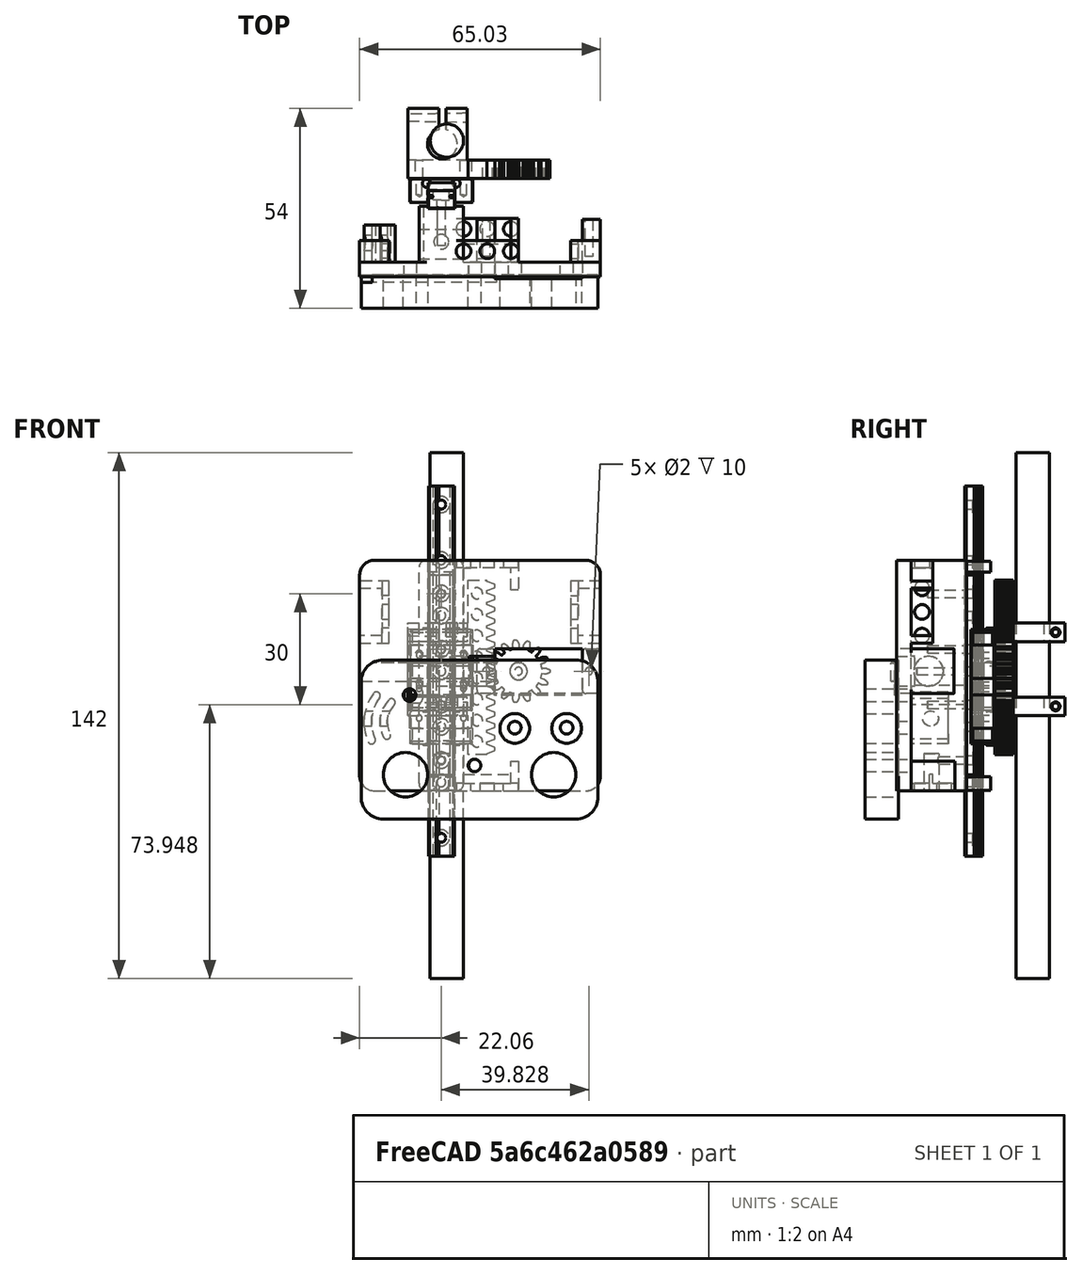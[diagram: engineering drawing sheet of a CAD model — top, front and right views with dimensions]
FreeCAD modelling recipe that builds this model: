
FCSTD DOCUMENT  (FreeCAD 1.0R39109 (Git))
Label: pen_plotter_head
License: All rights reserved
LicenseURL: https://en.wikipedia.org/wiki/All_rights_reserved
objects: Sketcher::SketchObject×36, PartDesign::Pocket×24, PartDesign::Pad×11, Part::Feature×10, PartDesign::LinearPattern×8, PartDesign::Body×4, App::Part×2, Mesh::Feature×2, Part::FeaturePython×2, Part::Box×2, PartDesign::FeatureBase×2, Part::MultiCommon×1, Part::MultiFuse×1, Part::Cylinder×1, PartDesign::PolarPattern×1
note: 220 computed .brp shape members not serialized (recipe doc carries the construction recipe); baked Part::Feature solids carry a one-line shape summary decoded from their .brp

FEATURE [Part::Feature] Part__Feature  label="Carriage-LWL7B"
  Placement = pos=(0,1.55,0.331361) rot=(0,0,1;0rad)
  shape: bbox 16.95 x 6.5 x 13.5 mm, 45 faces (baked)
FEATURE [Part::Feature] Part__Feature001  label="Carriage-LWL7B001"
  Placement = pos=(0,1.55,0.331361) rot=(0,0,1;0rad)
  shape: bbox 16.69 x 6.37 x 3.45 mm, 29 faces (baked)
FEATURE [Part::Feature] Part__Feature002  label="Carriage-LWL7B002"
  Placement = pos=(0,1.55,0.331361) rot=(0,0,1;0rad)
  shape: bbox 16.69 x 6.37 x 0.7 mm, 29 faces (baked)
FEATURE [Part::Feature] Part__Feature003  label="Carriage-LWL7B003"
  Placement = pos=(0,1.55,0.331361) rot=(0,0,1;0rad)
  shape: bbox 2.381 x 2.381 x 0.4 mm, 6 faces (baked)
FEATURE [Part::Feature] Part__Feature004  label="Carriage-LWL7B004"
  Placement = pos=(0,1.55,0.331361) rot=(0,0,1;0rad)
  shape: bbox 2.381 x 2.381 x 0.4 mm, 6 faces (baked)
FEATURE [Part::Feature] Part__Feature005  label="Carriage-LWL7B005"
  Placement = pos=(0,1.55,0.331361) rot=(0,0,1;0rad)
  shape: bbox 16.69 x 6.37 x 3.45 mm, 29 faces (baked)
FEATURE [Part::Feature] Part__Feature006  label="Carriage-LWL7B006"
  Placement = pos=(0,1.55,0.331361) rot=(0,0,1;0rad)
  shape: bbox 16.69 x 6.37 x 0.7 mm, 29 faces (baked)
FEATURE [Part::Feature] Part__Feature007  label="Carriage-LWL7B007"
  Placement = pos=(0,1.55,0.331361) rot=(0,0,1;0rad)
  shape: bbox 2.381 x 2.381 x 0.4 mm, 6 faces (baked)
FEATURE [Part::Feature] Part__Feature008  label="Carriage-LWL7B008"
  Placement = pos=(0,1.55,0.331361) rot=(0,0,1;0rad)
  shape: bbox 2.381 x 2.381 x 0.4 mm, 6 faces (baked)
FEATURE [App::Part] Carriage_LWL7B  label="Carriage-LWL7B009"
  Group = -> [Part__Feature,Part__Feature001,Part__Feature002,Part__Feature003,Part__Feature004,Part__Feature005,Part__Feature006,Part__Feature007,Part__Feature008]
  Origin = -> Origin
FEATURE [Part::Feature] Part__Feature009  label="LinearRail-LWL7B-100mm"
  shape: bbox 7 x 4.8 x 100 mm, 60 faces (baked)
FEATURE [App::Part] LinearRail_LWL7B_Assy  label="LinearRail-LWL7B-Assy"
  Group = -> [Carriage_LWL7B,Part__Feature009]
  Origin = -> Origin001
FEATURE [Mesh::Feature] Servo_SG90  label="Servo-SG90"
  Placement = pos=(37.5,-19,8.9e-15) rot=(0.57735,-0.57735,-0.57735;4.18879rad)
FEATURE [Part::FeaturePython] InvoluteRack  # WARN: FeaturePython — macro-defined, semantics opaque (R4)
  AttacherType = Attacher::AttachEngine3D
  Placement = pos=(11.5,25,-21) rot=(1,0,0;1.5708rad)
  add_endings = true
  beta = 0
  clearance = 0.25
  double_helix = false
  head = 0
  head_fillet = 0
  height = 5
  module = 1
  num_teeth = 15
  pressure_angle = 20
  properties_from_tool = false
  root_fillet = 0
  simplified = false
  thickness = 5
  transverse_pitch = 3.14159
  version = 1.3.0
FEATURE [Part::FeaturePython] InvoluteGear  # WARN: FeaturePython — macro-defined, semantics opaque (R4)
  AttacherType = Attacher::AttachEngine3D
  Placement = pos=(19,25.15,-2) rot=(1,0,0;1.5708rad)
  angular_backlash = 0
  backlash = 0
  beta = 0
  clearance = 0.25
  da = 17
  df = 12.5
  double_helix = false
  dw = 15
  head = 0
  head_fillet = 0
  height = 5
  module = 1
  num_teeth = 15
  numpoints = 20
  pressure_angle = 20
  properties_from_tool = false
  reversed_backlash = false
  root_fillet = 0
  shift = 0
  simple = false
  transverse_pitch = 3.14159
  traverse_module = 1
  undercut = false
  version = 1.3.0
  expr: angular_backlash = backlash / dw * 360 ° / pi
FEATURE [Mesh::Feature] Carriage_Plate_w_Threads
  Placement = pos=(-21.5,-48,24.5) rot=(-1,0,0;1.5708rad)
FEATURE [Part::Box] Box  label="Cube"
  AttacherType = Attacher::AttachEngine3D
  Height = 54
  Length = 25
  Placement = pos=(-13,-6,-19) rot=(0,0,1;0rad)
  Width = 25
FEATURE [Part::MultiCommon] Common
  Placement = pos=(0,0,-9) rot=(0,0,1;0rad)
  Refine = true
  Shapes = -> [LinearRail_LWL7B_Assy,Box]
FEATURE [Part::Box] Box001  label="Cube001"
  AttacherType = Attacher::AttachEngine3D
  Height = 25
  Length = 20
  Placement = pos=(-11,20,-12) rot=(0,0,1;0rad)
  Width = 5
FEATURE [Part::MultiFuse] Fusion
  Placement = pos=(1.6,-12,-5) rot=(0,0,1;0rad)
  Refine = true
  Shapes = -> [Box001,InvoluteRack]
FEATURE [Part::Cylinder] Cylinder  label="Pen"
  Angle = 360
  AttacherType = Attacher::AttachEngine3D
  FirstAngle = 0
  Height = 142
  Placement = pos=(1.5,18.25,-83) rot=(0,0,1;0rad)
  Radius = 4.5
  SecondAngle = 0
FEATURE [PartDesign::FeatureBase] BaseFeature
  BaseFeature = -> InvoluteGear
  Suppressed = false
FEATURE [Sketcher::SketchObject] Sketch
  ArcFitTolerance = 1e-06
  AttachmentSupport = -> [BaseFeature]
  FullyConstrained = true
  MakeInternals = false
  MapMode = 5
  Placement = pos=(0,0,0) rot=(1,0,0;3.14159rad)
  sketch-geometry (1):
    g0: Circle CenterX=0 CenterY=0 CenterZ=0 NormalX=0 NormalY=0 NormalZ=1 AngleXU=0 Radius=2.35
  constraints (2):
    c: Diameter(g0) = 4.7
    c: Coincident(g0,g-1)
FEATURE [PartDesign::Pocket] Pocket
  BaseFeature = -> BaseFeature
  Direction = (0,0,1)
  Length = 3
  Length2 = 5
  Profile = -> Sketch
  ReferenceAxis = -> Sketch [N_Axis]
  Refine = true
  Suppressed = false
  Type = 0
FEATURE [Sketcher::SketchObject] Sketch001
  ArcFitTolerance = 1e-06
  AttachmentSupport = -> [Pocket]
  FullyConstrained = true
  MakeInternals = false
  MapMode = 5
  Placement = pos=(0,0,3) rot=(1,0,0;3.14159rad)
  sketch-geometry (1):
    g0: Circle CenterX=0 CenterY=0 CenterZ=0 NormalX=0 NormalY=0 NormalZ=1 AngleXU=0 Radius=1.05
  constraints (2):
    c: Coincident(g0,g-1)
    c: Diameter(g0) = 2.1
FEATURE [PartDesign::Pocket] Pocket001
  BaseFeature = -> Pocket
  Direction = (0,0,1)
  Length = 2
  Length2 = 5
  Profile = -> Sketch001
  ReferenceAxis = -> Sketch001 [N_Axis]
  Refine = true
  Suppressed = false
  Type = 0
FEATURE [Sketcher::SketchObject] Sketch002
  ArcFitTolerance = 1e-06
  AttachmentSupport = -> [Pocket001]
  ExternalGeometry = -> [Pocket001]
  FullyConstrained = false
  MakeInternals = false
  MapMode = 5
  Placement = pos=(0,0,3) rot=(1,0,0;3.14159rad)
  sketch-geometry (5):
    g0: LineSegment StartX=-0.0912562 StartY=-2.35 StartZ=0 EndX=0.0912562 EndY=-2.35 EndZ=0
    g1: LineSegment StartX=0.0912562 StartY=-2.35 StartZ=0 EndX=0 EndY=-2.19194 EndZ=0
    g2: LineSegment StartX=0 StartY=-2.19194 StartZ=0 EndX=-0.0912562 EndY=-2.35 EndZ=0
    g3: Circle [constr] CenterX=0 CenterY=-2.29731 CenterZ=0 NormalX=0 NormalY=0 NormalZ=1 AngleXU=0 Radius=0.105374
    g4: GeomPoint X=0 Y=-2.35 Z=0
  constraints (12):
    c: Coincident(g0,g1)
    c: Coincident(g1,g2)
    c: Coincident(g2,g0)
    c: Equal(g0,g1)
    c: Equal(g0,g2)
    c: PointOnObject(g0,g3)
    c: PointOnObject(g1,g3)
    c: PointOnObject(g2,g3)
    c: PointOnObject(g1,g-2)
    c: Horizontal(g0)
    c: Symmetric(g0,g0,g4)
    c: PointOnObject(g4,g-3)
FEATURE [PartDesign::Pad] Pad
  BaseFeature = -> Pocket001
  Direction = (0,0,-1)
  Length = 3
  Length2 = 10
  Profile = -> Sketch002
  ReferenceAxis = -> Sketch002 [N_Axis]
  Refine = true
  Suppressed = false
  Type = 0
FEATURE [PartDesign::PolarPattern] PolarPattern
  Angle = 360
  Axis = -> Sketch002 [N_Axis]
  BaseFeature = -> Pad
  Mode = 0
  Occurrences = 21
  Offset = 120
  Originals = -> [Pad]
  Refine = true
  Suppressed = false
  TransformMode = 0
FEATURE [PartDesign::Body] Body  label="Gear"
  AllowCompound = false
  BaseFeature = -> InvoluteGear
  Group = -> [BaseFeature,Sketch,Pocket,Sketch001,Pocket001,Sketch002,Pad,PolarPattern]
  Origin = -> Origin002
  Placement = pos=(20.85,8,-1.8e-15) rot=(1,0,0;4.71239rad)
  Tip = -> PolarPattern
FEATURE [Sketcher::SketchObject] Sketch003
  ArcFitTolerance = 1e-06
  AttachmentSupport = -> [XZ_Plane003]
  FullyConstrained = false
  MakeInternals = false
  MapMode = 5
  Placement = pos=(0,0,0) rot=(1,0,0;1.5708rad)
  sketch-geometry (10):
    g0: LineSegment StartX=-18.0551 StartY=-32.3284 StartZ=0 EndX=38.9721 EndY=-32.3284 EndZ=0
    g1: LineSegment StartX=42.9721 StartY=-28.3284 StartZ=0 EndX=42.9721 EndY=25.9481 EndZ=0
    g2: LineSegment StartX=38.9721 StartY=29.9481 StartZ=0 EndX=-18.0551 EndY=29.9481 EndZ=0
    g3: LineSegment StartX=-22.0551 StartY=25.9481 StartZ=0 EndX=-22.0551 EndY=-28.3284 EndZ=0
    g4: ArcOfCircle CenterX=-18.0551 CenterY=-28.3284 CenterZ=0 NormalX=0 NormalY=0 NormalZ=1 AngleXU=0 Radius=4 StartAngle=3.14159 EndAngle=4.71239
    g5: ArcOfCircle CenterX=38.9721 CenterY=-28.3284 CenterZ=0 NormalX=0 NormalY=0 NormalZ=1 AngleXU=0 Radius=4 StartAngle=4.71239 EndAngle=6.28319
    g6: ArcOfCircle CenterX=38.9721 CenterY=25.9481 CenterZ=0 NormalX=0 NormalY=0 NormalZ=1 AngleXU=0 Radius=4 StartAngle=0 EndAngle=1.5708
    g7: ArcOfCircle CenterX=-18.0551 CenterY=25.9481 CenterZ=0 NormalX=0 NormalY=0 NormalZ=1 AngleXU=0 Radius=4 StartAngle=1.5708 EndAngle=3.14159
    g8: GeomPoint [constr] X=-22.0551 Y=-32.3284 Z=0
    g9: GeomPoint [constr] X=42.9721 Y=29.9481 Z=0
  constraints (20):
    c: Tangent(g0,g4) = -1.5708
    c: Tangent(g0,g5) = -1.5708
    c: Tangent(g1,g5) = -1.5708
    c: Tangent(g1,g6) = -1.5708
    c: Tangent(g2,g6) = -1.5708
    c: Tangent(g2,g7) = -1.5708
    c: Tangent(g3,g7) = -1.5708
    c: Tangent(g3,g4) = -1.5708
    c: Horizontal(g0)
    c: Horizontal(g2)
    c: Vertical(g1)
    c: Vertical(g3)
    c: Equal(g4,g5)
    c: Equal(g5,g6)
    c: Equal(g6,g7)
    c: PointOnObject(g8,g0)
    c: PointOnObject(g8,g3)
    c: PointOnObject(g9,g1)
    c: PointOnObject(g9,g2)
    c: Radius(g5) = 4
FEATURE [PartDesign::Pad] Pad001
  Direction = (0,-1,2e-16)
  Length = 4
  Length2 = 10
  Placement = pos=(0,0,0) rot=(1,0,0;1.5708rad)
  Profile = -> Sketch003
  ReferenceAxis = -> Sketch003 [N_Axis]
  Refine = true
  Suppressed = false
  Type = 0
FEATURE [Sketcher::SketchObject] Sketch004
  ArcFitTolerance = 1e-06
  AttachmentSupport = -> [Pad001]
  FullyConstrained = false
  MakeInternals = false
  MapMode = 5
  Placement = pos=(0,-3e-16,0) rot=(-1,0,0;1.5708rad)
  sketch-geometry (4):
    g0: LineSegment StartX=14.4828 StartY=6.05835 StartZ=0 EndX=14.4828 EndY=-6.05666 EndZ=0
    g1: LineSegment StartX=14.4828 StartY=-6.05666 StartZ=0 EndX=38.0765 EndY=-6.05666 EndZ=0
    g2: LineSegment StartX=38.0765 StartY=-6.05666 StartZ=0 EndX=38.0765 EndY=6.05835 EndZ=0
    g3: LineSegment StartX=38.0765 StartY=6.05835 StartZ=0 EndX=14.4828 EndY=6.05835 EndZ=0
  constraints (8):
    c: Coincident(g0,g1)
    c: Coincident(g1,g2)
    c: Coincident(g2,g3)
    c: Coincident(g3,g0)
    c: Vertical(g0)
    c: Vertical(g2)
    c: Horizontal(g1)
    c: Horizontal(g3)
FEATURE [PartDesign::Pocket] Pocket002
  BaseFeature = -> Pad001
  Direction = (0,-1,-2e-16)
  Length = 5
  Length2 = 5
  Placement = pos=(0,0,0) rot=(1,0,0;1.5708rad)
  Profile = -> Sketch004
  ReferenceAxis = -> Sketch004 [N_Axis]
  Refine = true
  Suppressed = false
  Type = 0
FEATURE [Sketcher::SketchObject] Sketch005
  ArcFitTolerance = 1e-06
  AttachmentSupport = -> [Pocket002]
  ExternalGeometry = -> [Pocket002]
  FullyConstrained = false
  MakeInternals = false
  MapMode = 5
  Placement = pos=(0,-3e-16,0) rot=(-1,0,0;1.5708rad)
  sketch-geometry (22):
    g0: LineSegment StartX=41.9721 StartY=6.05835 StartZ=0 EndX=39.0765 EndY=6.05835 EndZ=0
    g1: LineSegment StartX=38.0765 StartY=5.05835 StartZ=0 EndX=38.0765 EndY=-5.05666 EndZ=0
    g2: LineSegment StartX=39.0765 StartY=-6.05666 StartZ=0 EndX=41.9721 EndY=-6.05666 EndZ=0
    g3: LineSegment StartX=42.9721 StartY=-5.05666 StartZ=0 EndX=42.9721 EndY=5.05835 EndZ=0
    g4: ArcOfCircle CenterX=41.9721 CenterY=5.05835 CenterZ=0 NormalX=0 NormalY=0 NormalZ=1 AngleXU=0 Radius=1 StartAngle=0 EndAngle=1.5708
    g5: ArcOfCircle CenterX=39.0765 CenterY=5.05835 CenterZ=0 NormalX=0 NormalY=0 NormalZ=1 AngleXU=0 Radius=1 StartAngle=1.5708 EndAngle=3.14159
    g6: ArcOfCircle CenterX=39.0765 CenterY=-5.05666 CenterZ=0 NormalX=0 NormalY=0 NormalZ=1 AngleXU=0 Radius=1 StartAngle=3.14159 EndAngle=4.71239
    g7: ArcOfCircle CenterX=41.9721 CenterY=-5.05666 CenterZ=0 NormalX=0 NormalY=0 NormalZ=1 AngleXU=0 Radius=1 StartAngle=4.71239 EndAngle=6.28319
    g8: GeomPoint [constr] X=42.9721 Y=6.05835 Z=0
    g9: GeomPoint [constr] X=38.0765 Y=-6.05666 Z=0
    g10: LineSegment StartX=14.4828 StartY=-5.05666 StartZ=0 EndX=14.4828 EndY=5.05835 EndZ=0
    g11: LineSegment StartX=13.4828 StartY=6.05835 StartZ=0 EndX=10.5872 EndY=6.05835 EndZ=0
    g12: LineSegment StartX=9.58719 StartY=5.05835 StartZ=0 EndX=9.58719 EndY=-5.05666 EndZ=0
    g13: LineSegment StartX=10.5872 StartY=-6.05666 StartZ=0 EndX=13.4828 EndY=-6.05666 EndZ=0
    g14: ArcOfCircle CenterX=13.4828 CenterY=-5.05666 CenterZ=0 NormalX=0 NormalY=0 NormalZ=1 AngleXU=0 Radius=1 StartAngle=4.71239 EndAngle=6.28319
    g15: ArcOfCircle CenterX=13.4828 CenterY=5.05835 CenterZ=0 NormalX=0 NormalY=0 NormalZ=1 AngleXU=0 Radius=1 StartAngle=0 EndAngle=1.5708
    g16: ArcOfCircle CenterX=10.5872 CenterY=5.05835 CenterZ=0 NormalX=0 NormalY=0 NormalZ=1 AngleXU=0 Radius=1 StartAngle=1.5708 EndAngle=3.14159
    g17: ArcOfCircle CenterX=10.5872 CenterY=-5.05666 CenterZ=0 NormalX=0 NormalY=0 NormalZ=1 AngleXU=0 Radius=1 StartAngle=3.14159 EndAngle=4.71239
    g18: GeomPoint [constr] X=14.4828 Y=-6.05666 Z=0
    g19: GeomPoint [constr] X=9.58719 Y=6.05835 Z=0
    g20: LineSegment [constr] StartX=12.084 StartY=-6.05666 StartZ=0 EndX=39.8838 EndY=-6.05666 EndZ=0
    g21: LineSegment [constr] StartX=24.5654 StartY=6.05835 StartZ=0 EndX=40.1569 EndY=6.05835 EndZ=0
  constraints (52):
    c: Tangent(g0,g4) = -1.5708
    c: Tangent(g0,g5) = -1.5708
    c: Tangent(g1,g5) = -1.5708
    c: Tangent(g1,g6) = -1.5708
    c: Tangent(g2,g6) = -1.5708
    c: Tangent(g2,g7) = -1.5708
    c: Tangent(g3,g7) = -1.5708
    c: Tangent(g3,g4) = -1.5708
    c: Horizontal(g0)
    c: Horizontal(g2)
    c: Vertical(g1)
    c: Vertical(g3)
    c: Equal(g4,g5)
    c: Equal(g5,g6)
    c: Equal(g6,g7)
    c: PointOnObject(g8,g0)
    c: PointOnObject(g8,g3)
    c: PointOnObject(g9,g1)
    c: PointOnObject(g9,g2)
    c: Radius(g5) = 1
    c: Tangent(g10,g14) = -1.5708
    c: Tangent(g10,g15) = -1.5708
    c: Tangent(g11,g15) = -1.5708
    c: Tangent(g11,g16) = -1.5708
    c: Tangent(g12,g16) = -1.5708
    c: Tangent(g12,g17) = -1.5708
    c: Tangent(g13,g17) = -1.5708
    c: Tangent(g13,g14) = -1.5708
    c: Vertical(g10)
    c: Vertical(g12)
    c: Horizontal(g11)
    c: Horizontal(g13)
    c: Equal(g14,g15)
    c: Equal(g15,g16)
    c: Equal(g16,g17)
    c: PointOnObject(g18,g10)
    c: PointOnObject(g18,g13)
    c: PointOnObject(g19,g11)
    c: PointOnObject(g19,g12)
    c: Radius(g15) = 1
    c: Equal(g13,g2)
    c: Equal(g10,g1)
    c: PointOnObject(g10,g-4)
    c: PointOnObject(g1,g-3)
    c: PointOnObject(g3,g-5)
    c: PointOnObject(g20,g-6)
    c: Horizontal(g20)
    c: PointOnObject(g13,g20)
    c: PointOnObject(g2,g20)
    c: PointOnObject(g21,g-7)
    c: PointOnObject(g21,g-7)
    c: PointOnObject(g0,g21)
FEATURE [PartDesign::Pad] Pad002
  BaseFeature = -> Pocket002
  Direction = (0,1,2e-16)
  Length = 11.5
  Length2 = 10
  Placement = pos=(0,0,0) rot=(1,0,0;1.5708rad)
  Profile = -> Sketch005
  ReferenceAxis = -> Sketch005 [N_Axis]
  Refine = true
  Suppressed = false
  Type = 0
FEATURE [Sketcher::SketchObject] Sketch006
  ArcFitTolerance = 1e-06
  AttachmentSupport = -> [Pad002]
  ExternalGeometry = -> [Pad002]
  FullyConstrained = true
  MakeInternals = false
  MapMode = 5
  Placement = pos=(0,-4,0) rot=(1,0,0;1.5708rad)
  sketch-geometry (4):
    g0: LineSegment StartX=7.48281 StartY=4 StartZ=0 EndX=7.48281 EndY=-4 EndZ=0
    g1: LineSegment StartX=7.48281 StartY=-4 StartZ=0 EndX=14.4828 EndY=-4 EndZ=0
    g2: LineSegment StartX=14.4828 StartY=-4 StartZ=0 EndX=14.4828 EndY=4 EndZ=0
    g3: LineSegment StartX=14.4828 StartY=4 StartZ=0 EndX=7.48281 EndY=4 EndZ=0
  constraints (12):
    c: Coincident(g0,g1)
    c: Coincident(g1,g2)
    c: Coincident(g2,g3)
    c: Coincident(g3,g0)
    c: Vertical(g0)
    c: Vertical(g2)
    c: Horizontal(g1)
    c: Horizontal(g3)
    c: PointOnObject(g2,g-3)
    c: Distance(g2,g-1) = 4
    c: Distance(g1,g-1) = 4
    c: DistanceX(g3,g3) = 7
FEATURE [PartDesign::Pocket] Pocket003
  BaseFeature = -> Pad002
  Direction = (0,1,-2e-16)
  Length = 5
  Length2 = 5
  Placement = pos=(0,0,0) rot=(1,0,0;1.5708rad)
  Profile = -> Sketch006
  ReferenceAxis = -> Sketch006 [N_Axis]
  Refine = true
  Suppressed = false
  Type = 0
FEATURE [Sketcher::SketchObject] Sketch007
  ArcFitTolerance = 1e-06
  AttachmentSupport = -> [Pocket003]
  ExternalGeometry = -> [Pocket003]
  FullyConstrained = true
  MakeInternals = false
  MapMode = 5
  Placement = pos=(0,-3e-16,0) rot=(-1,0,0;1.5708rad)
  sketch-geometry (10):
    g0: LineSegment StartX=-6 StartY=30.3284 StartZ=0 EndX=-6 EndY=-27.9481 EndZ=0
    g1: LineSegment StartX=-4 StartY=-29.9481 StartZ=0 EndX=4 EndY=-29.9481 EndZ=0
    g2: LineSegment StartX=6 StartY=-27.9481 StartZ=0 EndX=6 EndY=30.3284 EndZ=0
    g3: LineSegment StartX=4 StartY=32.3284 StartZ=0 EndX=-4 EndY=32.3284 EndZ=0
    g4: ArcOfCircle CenterX=-4 CenterY=30.3284 CenterZ=0 NormalX=0 NormalY=0 NormalZ=1 AngleXU=0 Radius=2 StartAngle=1.5708 EndAngle=3.14159
    g5: ArcOfCircle CenterX=-4 CenterY=-27.9481 CenterZ=0 NormalX=0 NormalY=0 NormalZ=1 AngleXU=0 Radius=2 StartAngle=3.14159 EndAngle=4.71239
    g6: ArcOfCircle CenterX=4 CenterY=-27.9481 CenterZ=0 NormalX=0 NormalY=0 NormalZ=1 AngleXU=0 Radius=2 StartAngle=4.71239 EndAngle=6.28319
    g7: ArcOfCircle CenterX=4 CenterY=30.3284 CenterZ=0 NormalX=0 NormalY=0 NormalZ=1 AngleXU=0 Radius=2 StartAngle=0 EndAngle=1.5708
    g8: GeomPoint [constr] X=-6 Y=32.3284 Z=0
    g9: GeomPoint [constr] X=6 Y=-29.9481 Z=0
  constraints (24):
    c: Tangent(g0,g4) = -1.5708
    c: Tangent(g0,g5) = -1.5708
    c: Tangent(g1,g5) = -1.5708
    c: Tangent(g1,g6) = -1.5708
    c: Tangent(g2,g6) = -1.5708
    c: Tangent(g2,g7) = -1.5708
    c: Tangent(g3,g7) = -1.5708
    c: Tangent(g3,g4) = -1.5708
    c: Vertical(g0)
    c: Vertical(g2)
    c: Horizontal(g1)
    c: Horizontal(g3)
    c: Equal(g4,g5)
    c: Equal(g5,g6)
    c: Equal(g6,g7)
    c: PointOnObject(g8,g0)
    c: PointOnObject(g8,g3)
    c: PointOnObject(g9,g1)
    c: PointOnObject(g9,g2)
    c: Radius(g5) = 2
    c: PointOnObject(g3,g-3)
    c: PointOnObject(g1,g-4)
    c: Distance(g-2,g2) = 6
    c: Distance(g-2,g0) = 6
FEATURE [PartDesign::Pad] Pad003
  BaseFeature = -> Pocket003
  Direction = (0,1,2e-16)
  Length = 15
  Length2 = 10
  Placement = pos=(0,0,0) rot=(1,0,0;1.5708rad)
  Profile = -> Sketch007
  ReferenceAxis = -> Sketch007 [N_Axis]
  Refine = true
  Suppressed = false
  Type = 0
FEATURE [Sketcher::SketchObject] Sketch008
  ArcFitTolerance = 1e-06
  AttachmentSupport = -> [Pad003]
  FullyConstrained = false
  MakeInternals = false
  MapMode = 5
  Placement = pos=(-6,0,0) rot=(0.707107,0,-0.707107;3.14159rad)
  sketch-geometry (1):
    g0: Circle CenterX=0 CenterY=-4.67716 CenterZ=0 NormalX=0 NormalY=0 NormalZ=1 AngleXU=0 Radius=4
  constraints (2):
    c: PointOnObject(g0,g-2)
    c: Diameter(g0) = 8
FEATURE [PartDesign::Pocket] Pocket004
  BaseFeature = -> Pad003
  Direction = (1,0,2e-16)
  Length = 12
  Length2 = 5
  Placement = pos=(0,0,0) rot=(1,0,0;1.5708rad)
  Profile = -> Sketch008
  ReferenceAxis = -> Sketch008 [N_Axis]
  Refine = true
  Suppressed = false
  Type = 0
FEATURE [Sketcher::SketchObject] Sketch009
  ArcFitTolerance = 1e-06
  AttachmentSupport = -> [Pocket004]
  FullyConstrained = false
  MakeInternals = false
  MapMode = 5
  Placement = pos=(0,0,29.9481) rot=(0,0,1;3.14159rad)
  sketch-geometry (4):
    g0: LineSegment StartX=-3.63498 StartY=-14.4346 StartZ=0 EndX=-3.63498 EndY=-15.0307 EndZ=0
    g1: LineSegment StartX=-3.63498 StartY=-15.0307 StartZ=0 EndX=3.61502 EndY=-15.0307 EndZ=0
    g2: LineSegment StartX=3.61502 StartY=-15.0307 StartZ=0 EndX=3.61502 EndY=-14.4346 EndZ=0
    g3: LineSegment StartX=3.61502 StartY=-14.4346 StartZ=0 EndX=-3.63498 EndY=-14.4346 EndZ=0
  constraints (9):
    c: Coincident(g0,g1)
    c: Coincident(g1,g2)
    c: Coincident(g2,g3)
    c: Coincident(g3,g0)
    c: Vertical(g0)
    c: Vertical(g2)
    c: Horizontal(g1)
    c: Horizontal(g3)
    c: DistanceX(g3,g3) = 7.25
FEATURE [PartDesign::Pocket] Pocket005
  BaseFeature = -> Pocket004
  Direction = (0,0,-1)
  Length = 1000
  Length2 = 5
  Placement = pos=(0,0,0) rot=(1,0,0;1.5708rad)
  Profile = -> Sketch009
  ReferenceAxis = -> Sketch009 [N_Axis]
  Refine = true
  Suppressed = false
  Type = 0
FEATURE [Sketcher::SketchObject] Sketch010
  ArcFitTolerance = 1e-06
  AttachmentSupport = -> [Pocket005]
  ExternalGeometry = -> [Pocket005]
  FullyConstrained = true
  MakeInternals = false
  MapMode = 5
  Placement = pos=(0,14.4346,-3.2e-15) rot=(-1,0,0;1.5708rad)
  sketch-geometry (1):
    g0: Circle CenterX=0 CenterY=-20.9481 CenterZ=0 NormalX=0 NormalY=0 NormalZ=1 AngleXU=0 Radius=1
  constraints (3):
    c: PointOnObject(g0,g-2)
    c: Distance(g0,g-3) = 9
    c: Diameter(g0) = 2
FEATURE [PartDesign::Pocket] Pocket006
  BaseFeature = -> Pocket005
  Direction = (0,-1,-2e-16)
  Length = 10
  Length2 = 5
  Placement = pos=(0,0,0) rot=(1,0,0;1.5708rad)
  Profile = -> Sketch010
  ReferenceAxis = -> Sketch010 [N_Axis]
  Refine = true
  Suppressed = false
  Type = 0
FEATURE [PartDesign::LinearPattern] LinearPattern
  BaseFeature = -> Pocket006
  Direction = -> Sketch010 [V_Axis]
  Length = 45
  Mode = 0
  Occurrences = 4
  Offset = 15
  Originals = -> [Pocket006]
  Placement = pos=(0,0,0) rot=(1,0,0;1.5708rad)
  Refine = true
  Suppressed = false
  TransformMode = 0
FEATURE [Sketcher::SketchObject] Sketch011
  ArcFitTolerance = 1e-06
  AttachmentSupport = -> [LinearPattern]
  FullyConstrained = false
  MakeInternals = false
  MapMode = 5
  Placement = pos=(0,11.5,0) rot=(-1,0,0;1.5708rad)
  sketch-geometry (2):
    g0: Circle CenterX=39.8284 CenterY=0 CenterZ=0 NormalX=0 NormalY=0 NormalZ=1 AngleXU=0 Radius=1
    g1: Circle CenterX=12.1284 CenterY=0 CenterZ=0 NormalX=0 NormalY=0 NormalZ=1 AngleXU=0 Radius=1
  constraints (5):
    c: PointOnObject(g0,g-1)
    c: Diameter(g0) = 2
    c: PointOnObject(g1,g-1)
    c: Equal(g1,g0)
    c: DistanceX(g1,g0) = 27.7
FEATURE [PartDesign::Pocket] Pocket007
  BaseFeature = -> LinearPattern
  Direction = (0,-1,-2e-16)
  Length = 10
  Length2 = 5
  Placement = pos=(0,0,0) rot=(1,0,0;1.5708rad)
  Profile = -> Sketch011
  ReferenceAxis = -> Sketch011 [N_Axis]
  Refine = true
  Suppressed = false
  Type = 0
FEATURE [Sketcher::SketchObject] Sketch012
  ArcFitTolerance = 1e-06
  AttachmentSupport = -> [Pocket007]
  ExternalGeometry = -> [Pocket007]
  FullyConstrained = false
  MakeInternals = false
  MapMode = 5
  Placement = pos=(0,-3e-16,0) rot=(-1,0,0;1.5708rad)
  sketch-geometry (33):
    g0: LineSegment StartX=42.9721 StartY=-7.59545 StartZ=0 EndX=42.9721 EndY=-9.59545 EndZ=0
    g1: LineSegment StartX=42.9721 StartY=-9.59545 StartZ=0 EndX=36.9721 EndY=-9.59545 EndZ=0
    g2: LineSegment StartX=36.9721 StartY=-9.59545 StartZ=0 EndX=36.9721 EndY=-22.3954 EndZ=0
    g3: LineSegment StartX=36.9721 StartY=-22.3954 StartZ=0 EndX=42.9721 EndY=-22.3954 EndZ=0
    g4: LineSegment StartX=42.9721 StartY=-22.3954 StartZ=0 EndX=42.9721 EndY=-24.3954 EndZ=0
    g5: LineSegment StartX=42.9721 StartY=-24.3954 StartZ=0 EndX=34.9721 EndY=-24.3954 EndZ=0
    g6: LineSegment StartX=34.9721 StartY=-24.3954 StartZ=0 EndX=34.9721 EndY=-7.59545 EndZ=0
    g7: LineSegment StartX=34.9721 StartY=-7.59545 StartZ=0 EndX=42.9721 EndY=-7.59545 EndZ=0
    g8: LineSegment StartX=-22.0551 StartY=-7.59545 StartZ=0 EndX=-14.0551 EndY=-7.59545 EndZ=0
    g9: LineSegment StartX=-14.0551 StartY=-7.59545 StartZ=0 EndX=-14.0551 EndY=-24.3954 EndZ=0
    g10: LineSegment StartX=-14.0551 StartY=-24.3954 StartZ=0 EndX=-22.0551 EndY=-24.3954 EndZ=0
    g11: LineSegment StartX=-22.0551 StartY=-24.3954 StartZ=0 EndX=-22.0551 EndY=-22.3954 EndZ=0
    g12: LineSegment StartX=-22.0551 StartY=-22.3954 StartZ=0 EndX=-16.0551 EndY=-22.3954 EndZ=0
    g13: LineSegment StartX=-16.0551 StartY=-22.3954 StartZ=0 EndX=-16.0551 EndY=-9.59545 EndZ=0
    g14: LineSegment StartX=-16.0551 StartY=-9.59545 StartZ=0 EndX=-22.0551 EndY=-9.59545 EndZ=0
    g15: LineSegment StartX=-22.0551 StartY=-9.59545 StartZ=0 EndX=-22.0551 EndY=-7.59545 EndZ=0
    g16: LineSegment [constr] StartX=42.9721 StartY=-24.3954 StartZ=0 EndX=-22.0551 EndY=-24.3954 EndZ=0
    g17: LineSegment StartX=4 StartY=32.3284 StartZ=0 EndX=4 EndY=24.3284 EndZ=0
    g18: LineSegment StartX=4 StartY=24.3284 StartZ=0 EndX=6 EndY=24.3284 EndZ=0
    g19: LineSegment StartX=6 StartY=24.3284 StartZ=0 EndX=6 EndY=30.3284 EndZ=0
    g20: LineSegment StartX=6 StartY=30.3284 StartZ=0 EndX=18.8 EndY=30.3284 EndZ=0
    g21: LineSegment StartX=18.8 StartY=30.3284 StartZ=0 EndX=18.8 EndY=24.3284 EndZ=0
    g22: LineSegment StartX=18.8 StartY=24.3284 StartZ=0 EndX=20.8 EndY=24.3284 EndZ=0
    g23: LineSegment StartX=4 StartY=32.3284 StartZ=0 EndX=20.8 EndY=32.3284 EndZ=0
    g24: LineSegment StartX=20.8 StartY=24.3284 StartZ=0 EndX=20.8 EndY=32.3284 EndZ=0
    g25: LineSegment StartX=4 StartY=-21.9481 StartZ=0 EndX=4 EndY=-29.9481 EndZ=0
    g26: LineSegment StartX=4 StartY=-29.9481 StartZ=0 EndX=20.8 EndY=-29.9481 EndZ=0
    g27: LineSegment StartX=20.8 StartY=-29.9481 StartZ=0 EndX=20.8 EndY=-21.9481 EndZ=0
    g28: LineSegment StartX=20.8 StartY=-21.9481 StartZ=0 EndX=18.8 EndY=-21.9481 EndZ=0
    g29: LineSegment StartX=18.8 StartY=-21.9481 StartZ=0 EndX=18.8 EndY=-27.9481 EndZ=0
    g30: LineSegment StartX=18.8 StartY=-27.9481 StartZ=0 EndX=6 EndY=-27.9481 EndZ=0
    g31: LineSegment StartX=6 StartY=-27.9481 StartZ=0 EndX=6 EndY=-21.9481 EndZ=0
    g32: LineSegment StartX=6 StartY=-21.9481 StartZ=0 EndX=4 EndY=-21.9481 EndZ=0
  constraints (98):
    c: Coincident(g0,g1)
    c: Horizontal(g1)
    c: Coincident(g1,g2)
    c: Coincident(g2,g3)
    c: Horizontal(g3)
    c: Coincident(g3,g4)
    c: Coincident(g4,g5)
    c: Coincident(g5,g6)
    c: Vertical(g6)
    c: Coincident(g6,g7)
    c: Coincident(g7,g0)
    c: PointOnObject(g0,g-3)
    c: PointOnObject(g0,g-3)
    c: PointOnObject(g3,g-3)
    c: PointOnObject(g4,g-3)
    c: Parallel(g-3,g2)
    c: Parallel(g3,g5)
    c: Parallel(g5,g7)
    c: Equal(g0,g4)
    c: DistanceY(g2,g2) = 12.8
    c: DistanceY(g6,g6) = 16.8
    c: Distance(g6,g2) = 2
    c: DistanceX(g3,g3) = 6
    c: Horizontal(g8)
    c: Coincident(g8,g9)
    c: Vertical(g9)
    c: Coincident(g9,g10)
    c: Horizontal(g10)
    c: Coincident(g10,g11)
    c: Vertical(g11)
    c: Coincident(g11,g12)
    c: Horizontal(g12)
    c: Coincident(g12,g13)
    c: Vertical(g13)
    c: Coincident(g13,g14)
    c: Horizontal(g14)
    c: Coincident(g14,g15)
    c: Coincident(g15,g8)
    c: Parallel(g15,g11)
    c: Equal(g15,g11)
    c: Equal(g11,g0)
    c: Equal(g13,g2)
    c: Equal(g8,g7)
    c: Equal(g14,g1)
    c: Equal(g12,g3)
    c: PointOnObject(g8,g-4)
    c: Coincident(g16,g4)
    c: PointOnObject(g16,g11)
    c: Horizontal(g16)
    c: PointOnObject(g9,g16)
    c: PointOnObject(g17,g-5)
    c: Vertical(g17)
    c: Coincident(g17,g18)
    c: Horizontal(g18)
    c: Coincident(g18,g19)
    c: Vertical(g19)
    c: Coincident(g19,g20)
    c: Horizontal(g20)
    c: Coincident(g20,g21)
    c: Vertical(g21)
    c: Coincident(g21,g22)
    c: Horizontal(g22)
    c: Equal(g20,g2)
    c: Coincident(g23,g17)
    c: PointOnObject(g23,g-5)
    c: Coincident(g24,g22)
    c: Coincident(g24,g23)
    c: Parallel(g24,g17)
    c: Equal(g22,g18)
    c: Equal(g6,g23)
    c: Equal(g24,g7)
    c: Equal(g19,g21)
    c: Distance(g23,g20) = 2
    c: Vertical(g25)
    c: Coincident(g25,g26)
    c: Horizontal(g26)
    c: Coincident(g26,g27)
    c: Vertical(g27)
    c: Coincident(g27,g28)
    c: Horizontal(g28)
    c: Coincident(g28,g29)
    c: Vertical(g29)
    c: Coincident(g29,g30)
    c: Horizontal(g30)
    c: Coincident(g30,g31)
    c: Vertical(g31)
    c: Coincident(g31,g32)
    c: Coincident(g32,g25)
    c: Equal(g29,g3)
    c: Equal(g3,g31)
    c: Equal(g6,g26)
    c: Equal(g30,g2)
    c: Equal(g32,g28)
    c: Parallel(g32,g28)
    c: Equal(g27,g10)
    c: PointOnObject(g25,g-6)
    c: PointOnObject(g18,g-7)
    c: PointOnObject(g31,g-7)
FEATURE [PartDesign::Pad] Pad004
  BaseFeature = -> Pocket007
  Direction = (0,1,2e-16)
  Length = 5.8
  Length2 = 10
  Placement = pos=(0,0,0) rot=(1,0,0;1.5708rad)
  Profile = -> Sketch012
  ReferenceAxis = -> Sketch012 [N_Axis]
  Refine = true
  Suppressed = false
  Type = 0
FEATURE [Sketcher::SketchObject] Sketch013
  ArcFitTolerance = 1e-06
  AttachmentSupport = -> [Pad004]
  ExternalGeometry = -> [Pad004]
  FullyConstrained = true
  MakeInternals = false
  MapMode = 5
  Placement = pos=(36.9721,0,0) rot=(0.707107,0,0.707107;3.14159rad)
  sketch-geometry (1):
    g0: Circle CenterX=9.59545 CenterY=-2.9 CenterZ=0 NormalX=0 NormalY=0 NormalZ=1 AngleXU=0 Radius=2
  constraints (4):
    c: Diameter(g0) = 4
    c: PointOnObject(g0,g-3)
    c: Distance(g-3) = 5.8
    c: DistanceY(g0,g-3) = 2.9
FEATURE [PartDesign::Pocket] Pocket008
  BaseFeature = -> Pad004
  Direction = (-1,0,2e-16)
  Length = 5
  Length2 = 5
  Placement = pos=(0,0,0) rot=(1,0,0;1.5708rad)
  Profile = -> Sketch013
  ReferenceAxis = -> Sketch013 [N_Axis]
  Refine = true
  Suppressed = false
  Type = 0
FEATURE [PartDesign::LinearPattern] LinearPattern001
  BaseFeature = -> Pocket008
  Direction = -> Sketch013 [H_Axis]
  Length = 12.8
  Mode = 0
  Occurrences = 3
  Offset = 6.4
  Originals = -> [Pocket008]
  Placement = pos=(0,0,0) rot=(1,0,0;1.5708rad)
  Refine = true
  Suppressed = false
  TransformMode = 0
FEATURE [Sketcher::SketchObject] Sketch014
  ArcFitTolerance = 1e-06
  AttachmentSupport = -> [LinearPattern001]
  ExternalGeometry = -> [LinearPattern001]
  FullyConstrained = true
  MakeInternals = false
  MapMode = 5
  Placement = pos=(-16.0551,0,0) rot=(0.707107,0,-0.707107;3.14159rad)
  sketch-geometry (1):
    g0: Circle CenterX=-22.3954 CenterY=-2.9 CenterZ=0 NormalX=0 NormalY=0 NormalZ=1 AngleXU=0 Radius=2
  constraints (2):
    c: Diameter(g0) = 4
    c: Symmetric(g-3,g-3,g0)
FEATURE [PartDesign::Pocket] Pocket009
  BaseFeature = -> LinearPattern001
  Direction = (1,0,2e-16)
  Length = 5
  Length2 = 5
  Placement = pos=(0,0,0) rot=(1,0,0;1.5708rad)
  Profile = -> Sketch014
  ReferenceAxis = -> Sketch014 [N_Axis]
  Refine = true
  Suppressed = false
  Type = 0
FEATURE [PartDesign::LinearPattern] LinearPattern002
  BaseFeature = -> Pocket009
  Direction = -> Sketch014 [H_Axis]
  Length = 12.8
  Mode = 0
  Occurrences = 3
  Offset = 6.4
  Originals = -> [Pocket009]
  Placement = pos=(0,0,0) rot=(1,0,0;1.5708rad)
  Refine = true
  Suppressed = false
  TransformMode = 0
FEATURE [Sketcher::SketchObject] Sketch015
  ArcFitTolerance = 1e-06
  AttachmentSupport = -> [LinearPattern002]
  ExternalGeometry = -> [LinearPattern002]
  FullyConstrained = true
  MakeInternals = false
  MapMode = 5
  Placement = pos=(0,0,-30.3284) rot=(0,0,1;3.14159rad)
  sketch-geometry (1):
    g0: Circle CenterX=-18.8 CenterY=-2.9 CenterZ=0 NormalX=0 NormalY=0 NormalZ=1 AngleXU=0 Radius=2
  constraints (2):
    c: Diameter(g0) = 4
    c: Symmetric(g-3,g-3,g0)
FEATURE [PartDesign::Pocket] Pocket010
  BaseFeature = -> LinearPattern002
  Direction = (0,0,-1)
  Length = 5
  Length2 = 5
  Placement = pos=(0,0,0) rot=(1,0,0;1.5708rad)
  Profile = -> Sketch015
  ReferenceAxis = -> Sketch015 [N_Axis]
  Refine = true
  Suppressed = false
  Type = 0
FEATURE [PartDesign::LinearPattern] LinearPattern003
  BaseFeature = -> Pocket010
  Direction = -> Sketch015 [H_Axis]
  Length = 12.8
  Mode = 0
  Occurrences = 3
  Offset = 6.4
  Originals = -> [Pocket010]
  Placement = pos=(0,0,0) rot=(1,0,0;1.5708rad)
  Refine = true
  Suppressed = false
  TransformMode = 0
FEATURE [Sketcher::SketchObject] Sketch016
  ArcFitTolerance = 1e-06
  AttachmentSupport = -> [LinearPattern003]
  ExternalGeometry = -> [LinearPattern003]
  FullyConstrained = true
  MakeInternals = false
  MapMode = 5
  Placement = pos=(0,0,27.9481) rot=(1,0,0;3.14159rad)
  sketch-geometry (1):
    g0: Circle CenterX=18.8 CenterY=-2.9 CenterZ=0 NormalX=0 NormalY=0 NormalZ=1 AngleXU=0 Radius=2
  constraints (2):
    c: Diameter(g0) = 4
    c: Symmetric(g-3,g-3,g0)
FEATURE [PartDesign::Pocket] Pocket011
  BaseFeature = -> LinearPattern003
  Direction = (0,0,1)
  Length = 5
  Length2 = 5
  Placement = pos=(0,0,0) rot=(1,0,0;1.5708rad)
  Profile = -> Sketch016
  ReferenceAxis = -> Sketch016 [N_Axis]
  Refine = true
  Suppressed = false
  Type = 0
FEATURE [PartDesign::LinearPattern] LinearPattern004
  BaseFeature = -> Pocket011
  Direction = -> Sketch016 [H_Axis]
  Length = 12.8
  Mode = 0
  Occurrences = 3
  Offset = 6.4
  Originals = -> [Pocket011]
  Placement = pos=(0,0,0) rot=(1,0,0;1.5708rad)
  Refine = true
  Reversed = true
  Suppressed = false
  TransformMode = 0
FEATURE [Sketcher::SketchObject] Sketch017
  ArcFitTolerance = 1e-06
  AttachmentSupport = -> [LinearPattern004]
  FullyConstrained = false
  MakeInternals = false
  MapMode = 5
  Placement = pos=(0,-3e-16,0) rot=(-1,0,0;1.5708rad)
  sketch-geometry (2):
    g0: Circle CenterX=33.8407 CenterY=15.2606 CenterZ=0 NormalX=0 NormalY=0 NormalZ=1 AngleXU=0 Radius=1.7
    g1: Circle CenterX=19.8407 CenterY=15.2606 CenterZ=0 NormalX=0 NormalY=0 NormalZ=1 AngleXU=0 Radius=1.7
  constraints (4):
    c: Diameter(g0) = 3.4
    c: Equal(g1,g0)
    c: DistanceX(g1,g0) = 14
    c: DistanceY(g1,g0) = 0
FEATURE [Sketcher::SketchObject] Sketch018
  ArcFitTolerance = 1e-06
  AttachmentSupport = -> [LinearPattern004]
  FullyConstrained = false
  MakeInternals = false
  MapMode = 5
  Placement = pos=(0,-3e-16,0) rot=(-1,0,0;1.5708rad)
  sketch-geometry (2):
    g0: Circle CenterX=9.10382 CenterY=25.4732 CenterZ=0 NormalX=0 NormalY=0 NormalZ=1 AngleXU=0 Radius=1.7
    g1: Circle CenterX=-8.39618 CenterY=6.47323 CenterZ=0 NormalX=0 NormalY=0 NormalZ=1 AngleXU=0 Radius=1.7
  constraints (4):
    c: Diameter(g0) = 3.4
    c: Equal(g1,g0)
    c: DistanceX(g1,g0) = 17.5
    c: DistanceY(g1,g0) = 19
FEATURE [PartDesign::Pocket] Pocket012
  BaseFeature = -> LinearPattern004
  Direction = (0,-1,-2e-16)
  Length = 5
  Length2 = 5
  Placement = pos=(0,0,0) rot=(1,0,0;1.5708rad)
  Profile = -> Sketch017
  ReferenceAxis = -> Sketch017 [N_Axis]
  Refine = true
  Suppressed = false
  Type = 0
FEATURE [PartDesign::Pocket] Pocket013
  BaseFeature = -> Pocket012
  Direction = (0,-1,-2e-16)
  Length = 5
  Length2 = 5
  Placement = pos=(0,0,0) rot=(1,0,0;1.5708rad)
  Profile = -> Sketch018
  ReferenceAxis = -> Sketch018 [N_Axis]
  Refine = true
  Suppressed = false
  Type = 0
FEATURE [Sketcher::SketchObject] Sketch020
  ArcFitTolerance = 1e-06
  AttachmentSupport = -> [Pocket013]
  ExternalGeometry = -> [Pocket013]
  FullyConstrained = true
  MakeInternals = false
  MapMode = 5
  Placement = pos=(0,5.8,0) rot=(-1,0,0;1.5708rad)
  sketch-geometry (6):
    g0: LineSegment StartX=4 StartY=32.3284 StartZ=0 EndX=20.8 EndY=32.3284 EndZ=0
    g1: LineSegment StartX=20.8 StartY=32.3284 StartZ=0 EndX=20.8 EndY=24.3284 EndZ=0
    g2: LineSegment StartX=20.8 StartY=24.3284 StartZ=0 EndX=18.8 EndY=24.3284 EndZ=0
    g3: LineSegment StartX=18.8 StartY=24.3284 StartZ=0 EndX=18.8 EndY=30.3284 EndZ=0
    g4: LineSegment StartX=18.8 StartY=30.3284 StartZ=0 EndX=6 EndY=30.3284 EndZ=0
    g5: LineSegment StartX=6 StartY=30.3284 StartZ=0 EndX=4 EndY=32.3284 EndZ=0
  constraints (12):
    c: Coincident(g-7,g0)
    c: Coincident(g0,g-7)
    c: Coincident(g0,g1)
    c: Coincident(g1,g-6)
    c: Coincident(g1,g2)
    c: Coincident(g2,g-5)
    c: Coincident(g2,g3)
    c: Coincident(g3,g-4)
    c: Coincident(g3,g4)
    c: Coincident(g4,g-3)
    c: Coincident(g4,g5)
    c: Coincident(g5,g0)
FEATURE [PartDesign::Pad] Pad006
  BaseFeature = -> Pocket013
  Direction = (0,1,2e-16)
  Length = 6
  Length2 = 10
  Placement = pos=(0,0,0) rot=(1,0,0;1.5708rad)
  Profile = -> Sketch020
  ReferenceAxis = -> Sketch020 [N_Axis]
  Refine = true
  Suppressed = false
  Type = 0
FEATURE [Sketcher::SketchObject] Sketch021
  ArcFitTolerance = 1e-06
  AttachmentSupport = -> [Pad006]
  ExternalGeometry = -> [Pad006]
  FullyConstrained = true
  MakeInternals = false
  MapMode = 5
  Placement = pos=(0,-8.5e-15,-30.3284) rot=(0,0,1;3.14159rad)
  sketch-geometry (1):
    g0: Circle CenterX=-18.8 CenterY=-8.9 CenterZ=0 NormalX=0 NormalY=0 NormalZ=1 AngleXU=0 Radius=2
  constraints (3):
    c: Diameter(g0) = 4
    c: PointOnObject(g0,g-3)
    c: Distance(g0,g-3) = 2.9
FEATURE [PartDesign::Pocket] Pocket014
  BaseFeature = -> Pad006
  Direction = (0,0,-1)
  Length = 5
  Length2 = 5
  Placement = pos=(0,0,0) rot=(1,0,0;1.5708rad)
  Profile = -> Sketch021
  ReferenceAxis = -> Sketch021 [N_Axis]
  Refine = true
  Suppressed = false
  Type = 0
FEATURE [PartDesign::LinearPattern] LinearPattern005
  BaseFeature = -> Pocket014
  Direction = -> Sketch021 [H_Axis]
  Length = 12.8
  Mode = 0
  Occurrences = 3
  Offset = 6.4
  Originals = -> [Pocket014]
  Placement = pos=(0,0,0) rot=(1,0,0;1.5708rad)
  Refine = true
  Suppressed = false
  TransformMode = 0
FEATURE [Sketcher::SketchObject] Sketch022
  ArcFitTolerance = 1e-06
  AttachmentSupport = -> [LinearPattern005]
  ExternalGeometry = -> [LinearPattern005]
  FullyConstrained = true
  MakeInternals = false
  MapMode = 5
  Placement = pos=(0,-8.5e-15,-30.3284) rot=(0,0,1;3.14159rad)
  sketch-geometry (4):
    g0: LineSegment StartX=-18.8 StartY=-4.9 StartZ=0 EndX=-18.8 EndY=-5.8 EndZ=0
    g1: LineSegment StartX=-18.8 StartY=-5.8 StartZ=0 EndX=-6 EndY=-5.8 EndZ=0
    g2: LineSegment StartX=-6 StartY=-5.8 StartZ=0 EndX=-6 EndY=-4.9 EndZ=0
    g3: LineSegment StartX=-6 StartY=-4.9 StartZ=0 EndX=-18.8 EndY=-4.9 EndZ=0
  constraints (11):
    c: Coincident(g0,g1)
    c: Coincident(g1,g2)
    c: Coincident(g2,g3)
    c: Coincident(g3,g0)
    c: Vertical(g0)
    c: Vertical(g2)
    c: Horizontal(g1)
    c: Horizontal(g3)
    c: Coincident(g0,g-4)
    c: PointOnObject(g1,g-3)
    c: Distance(g-6,g1) = 6
FEATURE [PartDesign::Pad] Pad007
  BaseFeature = -> LinearPattern005
  Direction = (0,0,1)
  Length = 2.5
  Length2 = 10
  Placement = pos=(0,0,0) rot=(1,0,0;1.5708rad)
  Profile = -> Sketch022
  ReferenceAxis = -> Sketch022 [N_Axis]
  Refine = true
  Suppressed = false
  Type = 0
FEATURE [Sketcher::SketchObject] Sketch023
  ArcFitTolerance = 1e-06
  AttachmentSupport = -> [Pad007]
  FullyConstrained = false
  MakeInternals = false
  MapMode = 5
  Placement = pos=(0,-3e-16,0) rot=(-1,0,0;1.5708rad)
  sketch-geometry (8):
    g0: ArcOfCircle CenterX=-7.85482 CenterY=13.7619 CenterZ=0 NormalX=0 NormalY=0 NormalZ=1 AngleXU=0 Radius=13.0171 StartAngle=2.72245 EndAngle=3.77866
    g1: ArcOfCircle CenterX=-17.5123 CenterY=6.61536 CenterZ=0 NormalX=0 NormalY=0 NormalZ=1 AngleXU=0 Radius=1.00294 StartAngle=3.77866 EndAngle=6.92026
    g2: ArcOfCircle CenterX=-18.829 CenterY=18.6514 CenterZ=0 NormalX=0 NormalY=0 NormalZ=1 AngleXU=0 Radius=1.00294 StartAngle=5.86404 EndAngle=9.00564
    g3: ArcOfCircle CenterX=-7.85482 CenterY=13.7619 CenterZ=0 NormalX=0 NormalY=0 NormalZ=1 AngleXU=0 Radius=11.0112 StartAngle=2.72245 EndAngle=3.77866
    g4: ArcOfCircle CenterX=-7.85482 CenterY=13.7619 CenterZ=0 NormalX=0 NormalY=0 NormalZ=1 AngleXU=0 Radius=8.71934 StartAngle=2.65637 EndAngle=3.90045
    g5: ArcOfCircle CenterX=-13.4561 CenterY=8.45028 CenterZ=0 NormalX=0 NormalY=0 NormalZ=1 AngleXU=0 Radius=1 StartAngle=3.90045 EndAngle=7.04204
    g6: ArcOfCircle CenterX=-14.6831 CenterY=17.3623 CenterZ=0 NormalX=0 NormalY=0 NormalZ=1 AngleXU=0 Radius=1 StartAngle=5.79796 EndAngle=8.93955
    g7: ArcOfCircle CenterX=-7.85482 CenterY=13.7619 CenterZ=0 NormalX=0 NormalY=0 NormalZ=1 AngleXU=0 Radius=6.71934 StartAngle=2.65637 EndAngle=3.90045
  constraints (12):
    c: Coincident(g0,g3)
    c: Tangent(g3,g2) = 1.5708
    c: Tangent(g3,g1) = 1.5708
    c: Tangent(g0,g2) = -1.5708
    c: Tangent(g0,g1) = -1.5708
    c: Coincident(g4,g7)
    c: Tangent(g7,g6) = 1.5708
    c: Tangent(g7,g5) = 1.5708
    c: Tangent(g4,g6) = -1.5708
    c: Tangent(g4,g5) = -1.5708
    c: Radius(g6) = 1
    c: Coincident(g4,g0)
FEATURE [PartDesign::Pad] Pad008
  BaseFeature = -> Pad007
  Direction = (0,1,2e-16)
  Length = 10
  Length2 = 10
  Placement = pos=(0,0,0) rot=(1,0,0;1.5708rad)
  Profile = -> Sketch023
  ReferenceAxis = -> Sketch023 [N_Axis]
  Refine = true
  Suppressed = false
  Type = 0
FEATURE [Sketcher::SketchObject] Sketch024
  ArcFitTolerance = 1e-06
  AttachmentSupport = -> [Pad008]
  FullyConstrained = false
  MakeInternals = false
  MapMode = 5
  Placement = pos=(-6,0,0) rot=(0.707107,0,-0.707107;3.14159rad)
  sketch-geometry (1):
    g0: Circle CenterX=12.7643 CenterY=-5.21997 CenterZ=0 NormalX=0 NormalY=0 NormalZ=1 AngleXU=0 Radius=2.09537
FEATURE [PartDesign::Pocket] Pocket015
  BaseFeature = -> Pad008
  Direction = (1,0,2e-16)
  Length = 100
  Length2 = 5
  Placement = pos=(0,0,0) rot=(1,0,0;1.5708rad)
  Profile = -> Sketch024
  ReferenceAxis = -> Sketch024 [N_Axis]
  Refine = true
  Reversed = true
  Suppressed = false
  Type = 0
FEATURE [Sketcher::SketchObject] Sketch025
  ArcFitTolerance = 1e-06
  AttachmentSupport = -> [Pocket015]
  ExternalGeometry = -> [Pocket015]
  FullyConstrained = true
  MakeInternals = false
  MapMode = 5
  Placement = pos=(0,-3e-16,0) rot=(-1,0,0;1.5708rad)
  sketch-geometry (1):
    g0: Circle CenterX=-8.39618 CenterY=6.47323 CenterZ=0 NormalX=0 NormalY=0 NormalZ=1 AngleXU=0 Radius=3.5
  constraints (2):
    c: Coincident(g0,g-3)
    c: Diameter(g0) = 7
FEATURE [PartDesign::Pocket] Pocket016
  BaseFeature = -> Pocket015
  Direction = (0,-1,-2e-16)
  Length = 25
  Length2 = 5
  Placement = pos=(0,0,0) rot=(1,0,0;1.5708rad)
  Profile = -> Sketch025
  ReferenceAxis = -> Sketch025 [N_Axis]
  Refine = true
  Reversed = true
  Suppressed = false
  Type = 0
FEATURE [Sketcher::SketchObject] Sketch026
  ArcFitTolerance = 1e-06
  AttachmentSupport = -> [Pocket016]
  FullyConstrained = false
  MakeInternals = false
  MapMode = 5
  Placement = pos=(0,0,-32.3284) rot=(1,0,0;3.14159rad)
  sketch-geometry (1):
    g0: Circle CenterX=0 CenterY=-5.44577 CenterZ=0 NormalX=0 NormalY=0 NormalZ=1 AngleXU=0 Radius=2
  constraints (2):
    c: PointOnObject(g0,g-2)
    c: Diameter(g0) = 4
FEATURE [PartDesign::Pocket] Pocket017
  BaseFeature = -> Pocket016
  Direction = (0,0,1)
  Length = 10
  Length2 = 5
  Placement = pos=(0,0,0) rot=(1,0,0;1.5708rad)
  Profile = -> Sketch026
  ReferenceAxis = -> Sketch026 [N_Axis]
  Refine = true
  Suppressed = false
  Type = 0
FEATURE [PartDesign::FeatureBase] BaseFeature001
  BaseFeature = -> Fusion
  Suppressed = false
FEATURE [Sketcher::SketchObject] Sketch028
  ArcFitTolerance = 1e-06
  AttachmentSupport = -> [BaseFeature001]
  ExternalGeometry = -> [BaseFeature001]
  FullyConstrained = false
  MakeInternals = false
  MapMode = 5
  Placement = pos=(-7.2e-15,25,0) rot=(0,0.707107,0.707107;3.14159rad)
  sketch-geometry (4):
    g0: Circle CenterX=8 CenterY=-3.5313 CenterZ=0 NormalX=0 NormalY=0 NormalZ=1 AngleXU=0 Radius=1.1
    g1: Circle CenterX=-4 CenterY=-3.5313 CenterZ=0 NormalX=0 NormalY=0 NormalZ=1 AngleXU=0 Radius=1.1
    g2: Circle CenterX=8 CenterY=4.4687 CenterZ=0 NormalX=0 NormalY=0 NormalZ=1 AngleXU=0 Radius=1.1
    g3: Circle CenterX=-4 CenterY=4.4687 CenterZ=0 NormalX=0 NormalY=0 NormalZ=1 AngleXU=0 Radius=1.1
  constraints (11):
    c: Diameter(g0) = 2.2
    c: Diameter(g1) = 2.2
    c: Diameter(g2) = 2.2
    c: Diameter(g3) = 2.2
    c: DistanceY(g2,g3) = 0
    c: DistanceY(g1,g0) = 0
    c: DistanceX(g3,g1) = 0
    c: DistanceX(g2,g0) = 0
    c: DistanceX(g3,g2) = 12
    c: DistanceY(g0,g2) = 8
    c: Distance(g2,g-3) = 3
FEATURE [PartDesign::Pocket] Pocket018
  BaseFeature = -> BaseFeature001
  Direction = (0,-1,2e-16)
  Length = 5
  Length2 = 5
  Profile = -> Sketch028
  ReferenceAxis = -> Sketch028 [N_Axis]
  Refine = true
  Suppressed = false
  Type = 0
FEATURE [Sketcher::SketchObject] Sketch029
  ArcFitTolerance = 1e-06
  AttachmentSupport = -> [Pocket018]
  FullyConstrained = false
  MakeInternals = false
  MapMode = 5
  Placement = pos=(-5.8e-15,20,0) rot=(1,0,0;1.5708rad)
  sketch-geometry (1):
    g0: Circle CenterX=7.62764 CenterY=21.0303 CenterZ=0 NormalX=0 NormalY=0 NormalZ=1 AngleXU=0 Radius=1.5
  constraints (1):
    c: Diameter(g0) = 3
FEATURE [PartDesign::Pocket] Pocket019
  BaseFeature = -> Pocket018
  Direction = (0,1,-2e-16)
  Length = 5
  Length2 = 5
  Profile = -> Sketch029
  ReferenceAxis = -> Sketch029 [N_Axis]
  Refine = true
  Suppressed = false
  Type = 0
FEATURE [PartDesign::LinearPattern] LinearPattern006
  BaseFeature = -> Pocket019
  Direction = -> Sketch029 [V_Axis]
  Length = 40
  Mode = 0
  Occurrences = 8
  Offset = 5.71429
  Originals = -> [Pocket019]
  Refine = true
  Reversed = true
  Suppressed = false
  TransformMode = 0
FEATURE [Sketcher::SketchObject] Sketch030
  ArcFitTolerance = 1e-06
  AttachmentSupport = -> [LinearPattern006]
  ExternalGeometry = -> [LinearPattern006]
  FullyConstrained = true
  MakeInternals = false
  MapMode = 5
  Placement = pos=(-7.2e-15,25,0) rot=(0,0.707107,0.707107;3.14159rad)
  sketch-geometry (8):
    g0: LineSegment StartX=11 StartY=-12 StartZ=0 EndX=-5 EndY=-12 EndZ=0
    g1: LineSegment StartX=-5 StartY=-12 StartZ=0 EndX=-5 EndY=-7 EndZ=0
    g2: LineSegment StartX=-5 StartY=-7 StartZ=0 EndX=11 EndY=-7 EndZ=0
    g3: LineSegment StartX=11 StartY=-7 StartZ=0 EndX=11 EndY=-12 EndZ=0
    g4: LineSegment StartX=11 StartY=13 StartZ=0 EndX=-5 EndY=13 EndZ=0
    g5: LineSegment StartX=-5 StartY=13 StartZ=0 EndX=-5 EndY=8 EndZ=0
    g6: LineSegment StartX=-5 StartY=8 StartZ=0 EndX=11 EndY=8 EndZ=0
    g7: LineSegment StartX=11 StartY=8 StartZ=0 EndX=11 EndY=13 EndZ=0
  constraints (24):
    c: Coincident(g0,g1)
    c: Coincident(g1,g2)
    c: Coincident(g2,g3)
    c: Coincident(g3,g0)
    c: Horizontal(g0)
    c: Horizontal(g2)
    c: Vertical(g1)
    c: Vertical(g3)
    c: Coincident(g4,g5)
    c: Coincident(g5,g6)
    c: Coincident(g6,g7)
    c: Coincident(g7,g4)
    c: Horizontal(g4)
    c: Horizontal(g6)
    c: Vertical(g5)
    c: Vertical(g7)
    c: Equal(g3,g7)
    c: Equal(g2,g4)
    c: DistanceY(g7,g7) = 5
    c: DistanceX(g2,g2) = 16
    c: PointOnObject(g0,g-5)
    c: PointOnObject(g2,g-3)
    c: PointOnObject(g4,g-4)
    c: PointOnObject(g4,g-3)
FEATURE [PartDesign::Pad] Pad009
  BaseFeature = -> LinearPattern006
  Direction = (0,1,-2e-16)
  Length = 14
  Length2 = 10
  Profile = -> Sketch030
  ReferenceAxis = -> Sketch030 [N_Axis]
  Refine = true
  Suppressed = false
  Type = 0
FEATURE [Sketcher::SketchObject] Sketch031
  ArcFitTolerance = 1e-06
  AttachmentSupport = -> [Pad009]
  FullyConstrained = false
  MakeInternals = false
  MapMode = 5
  Placement = pos=(0,0,-12) rot=(1,0,0;3.14159rad)
  sketch-geometry (7):
    g0: LineSegment [constr] StartX=-1.71039 StartY=-20.1256 StartZ=0 EndX=-1.71039 EndY=-35.2194 EndZ=0
    g1: Circle CenterX=-1.71039 CenterY=-29.3342 CenterZ=0 NormalX=0 NormalY=0 NormalZ=1 AngleXU=0 Radius=4
    g2: LineSegment StartX=-0.748232 StartY=-39.3353 StartZ=0 EndX=-0.748232 EndY=-31.0472 EndZ=0
    g3: LineSegment StartX=-0.748232 StartY=-31.0472 StartZ=0 EndX=-2.67254 EndY=-31.0472 EndZ=0
    g4: LineSegment StartX=-2.67254 StartY=-31.0472 StartZ=0 EndX=-2.67254 EndY=-39.3353 EndZ=0
    g5: LineSegment StartX=-2.67254 StartY=-39.3353 StartZ=0 EndX=-0.748232 EndY=-39.3353 EndZ=0
    g6: GeomPoint [constr] X=-1.71039 Y=-35.1912 Z=0
  constraints (13):
    c: Vertical(g0)
    c: Diameter(g1) = 8
    c: PointOnObject(g1,g0)
    c: Coincident(g2,g3)
    c: Coincident(g3,g4)
    c: Coincident(g4,g5)
    c: Coincident(g5,g2)
    c: Vertical(g2)
    c: Vertical(g4)
    c: Horizontal(g3)
    c: Horizontal(g5)
    c: Symmetric(g4,g2,g6)
    c: PointOnObject(g6,g0)
FEATURE [PartDesign::Pocket] Pocket020
  BaseFeature = -> Pad009
  Direction = (0,0,1)
  Length = 5000
  Length2 = 5
  Profile = -> Sketch031
  ReferenceAxis = -> Sketch031 [N_Axis]
  Refine = true
  Suppressed = false
  Type = 0
FEATURE [Sketcher::SketchObject] Sketch032
  ArcFitTolerance = 1e-06
  AttachmentSupport = -> [Pocket020]
  FullyConstrained = true
  MakeInternals = false
  MapMode = 5
  Placement = pos=(0,0,-12) rot=(1,0,0;3.14159rad)
FEATURE [Sketcher::SketchObject] Sketch033
  ArcFitTolerance = 1e-06
  AttachmentSupport = -> [Pocket020]
  ExternalGeometry = -> [Pocket020]
  FullyConstrained = true
  MakeInternals = false
  MapMode = 5
  Placement = pos=(5,0,0) rot=(0.57735,0.57735,0.57735;2.0944rad)
  sketch-geometry (1):
    g0: Circle CenterX=36.46 CenterY=-9.5 CenterZ=0 NormalX=0 NormalY=0 NormalZ=1 AngleXU=0 Radius=1.2
  constraints (3):
    c: Diameter(g0) = 2.4
    c: Distance(g0,g-3) = 2.5
    c: Distance(g0,g-5) = 2.54
FEATURE [PartDesign::Pocket] Pocket021
  BaseFeature = -> Pocket020
  Direction = (-1,0,0)
  Length = 20
  Length2 = 5
  Profile = -> Sketch033
  ReferenceAxis = -> Sketch033 [N_Axis]
  Refine = true
  Suppressed = false
  TaperAngle = -1
  Type = 0
FEATURE [PartDesign::LinearPattern] LinearPattern007
  BaseFeature = -> Pocket021
  Direction = -> Sketch033 [V_Axis]
  Length = 20
  Mode = 0
  Occurrences = 2
  Offset = 20
  Originals = -> [Pocket021]
  Refine = true
  Suppressed = false
  TransformMode = 0
FEATURE [PartDesign::Body] Body003  label="PenHolder"
  AllowCompound = false
  BaseFeature = -> Fusion
  Group = -> [BaseFeature001,Sketch028,Pocket018,Sketch029,Pocket019,LinearPattern006,Sketch030,Pad009,Sketch031,Pocket020,Sketch032,Sketch033,Pocket021,LinearPattern007]
  Origin = -> Origin005
  Placement = pos=(2,-12,0) rot=(0,0,1;0rad)
  Tip = -> LinearPattern007
FEATURE [Sketcher::SketchObject] Sketch034
  ArcFitTolerance = 1e-06
  AttachmentSupport = -> [XZ_Plane006]
  FullyConstrained = false
  MakeInternals = false
  MapMode = 5
  Placement = pos=(0,0,0) rot=(1,0,0;1.5708rad)
  sketch-geometry (16):
    g0: LineSegment StartX=38.8388 StartY=1.54731 StartZ=0 EndX=-13.1612 EndY=1.54731 EndZ=0
    g1: LineSegment StartX=-19.1612 StartY=-4.45269 StartZ=0 EndX=-19.1612 EndY=-35.4527 EndZ=0
    g2: LineSegment StartX=-13.1612 StartY=-41.4527 StartZ=0 EndX=38.8388 EndY=-41.4527 EndZ=0
    g3: LineSegment StartX=44.8388 StartY=-35.4527 StartZ=0 EndX=44.8388 EndY=-4.45269 EndZ=0
    g4: ArcOfCircle CenterX=38.8388 CenterY=-4.45269 CenterZ=0 NormalX=0 NormalY=0 NormalZ=1 AngleXU=0 Radius=6 StartAngle=0 EndAngle=1.5708
    g5: ArcOfCircle CenterX=-13.1612 CenterY=-4.45269 CenterZ=0 NormalX=0 NormalY=0 NormalZ=1 AngleXU=0 Radius=6 StartAngle=1.5708 EndAngle=3.14159
    g6: ArcOfCircle CenterX=-13.1612 CenterY=-35.4527 CenterZ=0 NormalX=0 NormalY=0 NormalZ=1 AngleXU=0 Radius=6 StartAngle=3.14159 EndAngle=4.71239
    g7: ArcOfCircle CenterX=38.8388 CenterY=-35.4527 CenterZ=0 NormalX=0 NormalY=0 NormalZ=1 AngleXU=0 Radius=6 StartAngle=4.71239 EndAngle=6.28319
    g8: GeomPoint [constr] X=44.8388 Y=1.54731 Z=0
    g9: GeomPoint [constr] X=-19.1612 Y=-41.4527 Z=0
    g10: Circle CenterX=32.8388 CenterY=-29.4527 CenterZ=0 NormalX=0 NormalY=0 NormalZ=1 AngleXU=0 Radius=6
    g11: Circle CenterX=-7.16125 CenterY=-29.4527 CenterZ=0 NormalX=0 NormalY=0 NormalZ=1 AngleXU=0 Radius=6
    g12: Circle CenterX=22.3388 CenterY=-16.9527 CenterZ=0 NormalX=0 NormalY=0 NormalZ=1 AngleXU=0 Radius=4
    g13: Circle CenterX=36.3388 CenterY=-16.9527 CenterZ=0 NormalX=0 NormalY=0 NormalZ=1 AngleXU=0 Radius=4
    g14: Circle CenterX=11.4388 CenterY=-26.9527 CenterZ=0 NormalX=0 NormalY=0 NormalZ=1 AngleXU=0 Radius=1.7
    g15: Circle CenterX=-6.06125 CenterY=-7.95269 CenterZ=0 NormalX=0 NormalY=0 NormalZ=1 AngleXU=0 Radius=1.7
  constraints (40):
    c: Tangent(g0,g4) = -1.5708
    c: Tangent(g0,g5) = -1.5708
    c: Tangent(g1,g5) = -1.5708
    c: Tangent(g1,g6) = -1.5708
    c: Tangent(g2,g6) = -1.5708
    c: Tangent(g2,g7) = -1.5708
    c: Tangent(g3,g7) = -1.5708
    c: Tangent(g3,g4) = -1.5708
    c: Horizontal(g0)
    c: Horizontal(g2)
    c: Vertical(g1)
    c: Vertical(g3)
    c: Equal(g4,g5)
    c: Equal(g5,g6)
    c: Equal(g6,g7)
    c: PointOnObject(g8,g0)
    c: PointOnObject(g8,g3)
    c: PointOnObject(g9,g1)
    c: PointOnObject(g9,g2)
    c: Radius(g5) = 6
    c: DistanceY(g2,g0) = 43
    c: DistanceX(g1,g3) = 64
    c: Equal(g10,g11)
    c: Diameter(g10) = 12
    c: DistanceY(g10,g11) = 0
    c: DistanceX(g11,g10) = 40
    c: DistanceY(g12,g13) = 0
    c: DistanceX(g12,g13) = 14
    c: Diameter(g13) = 8
    c: Equal(g12,g13)
    c: Equal(g14,g15)
    c: Diameter(g14) = 3.4
    c: DistanceX(g11,g15) = 1.1
    c: DistanceX(g15,g14) = 17.5
    c: DistanceY(g14,g15) = 19
    c: Distance(g14,g2) = 14.5
    c: Distance(g13,g2) = 24.5
    c: Distance(g11,g1) = 12
    c: Distance(g13,g3) = 8.5
    c: Distance(g11,g2) = 12
FEATURE [PartDesign::Pad] Pad010
  Direction = (0,-1,2e-16)
  Length = 9
  Length2 = 10
  Placement = pos=(0,0,0) rot=(1,0,0;1.5708rad)
  Profile = -> Sketch034
  ReferenceAxis = -> Sketch034 [N_Axis]
  Refine = true
  Suppressed = false
  Type = 0
FEATURE [Sketcher::SketchObject] Sketch035
  ArcFitTolerance = 1e-06
  AttachmentSupport = -> [Pad010]
  FullyConstrained = false
  MakeInternals = false
  MapMode = 5
  Placement = pos=(0,-4.7e-15,0) rot=(-1,0,0;1.5708rad)
  sketch-geometry (4):
    g0: LineSegment StartX=16.8486 StartY=8.08933 StartZ=0 EndX=16.8486 EndY=-8.26877 EndZ=0
    g1: LineSegment StartX=16.8486 StartY=-8.26877 StartZ=0 EndX=40.5267 EndY=-8.26877 EndZ=0
    g2: LineSegment StartX=40.5267 StartY=-8.26877 StartZ=0 EndX=40.5267 EndY=8.08933 EndZ=0
    g3: LineSegment StartX=40.5267 StartY=8.08933 StartZ=0 EndX=16.8486 EndY=8.08933 EndZ=0
  constraints (8):
    c: Coincident(g0,g1)
    c: Coincident(g1,g2)
    c: Coincident(g2,g3)
    c: Coincident(g3,g0)
    c: Vertical(g0)
    c: Vertical(g2)
    c: Horizontal(g1)
    c: Horizontal(g3)
FEATURE [PartDesign::Pocket] Pocket022
  BaseFeature = -> Pad010
  Direction = (0,-1,-2e-16)
  Length = 1
  Length2 = 5
  Placement = pos=(0,0,0) rot=(1,0,0;1.5708rad)
  Profile = -> Sketch035
  ReferenceAxis = -> Sketch035 [N_Axis]
  Refine = true
  Suppressed = false
  Type = 0
FEATURE [Sketcher::SketchObject] Sketch036
  ArcFitTolerance = 1e-06
  AttachmentSupport = -> [Pocket022]
  FullyConstrained = false
  MakeInternals = false
  MapMode = 5
  Placement = pos=(0,-4.7e-15,0) rot=(-1,0,0;1.5708rad)
  sketch-geometry (4):
    g0: LineSegment StartX=-20.5245 StartY=4.25992 StartZ=0 EndX=17.3424 EndY=4.25992 EndZ=0
    g1: LineSegment StartX=17.3424 StartY=4.25992 StartZ=0 EndX=17.3424 EndY=-0.740081 EndZ=0
    g2: LineSegment StartX=17.3424 StartY=-0.740081 StartZ=0 EndX=-20.5245 EndY=-0.740081 EndZ=0
    g3: LineSegment StartX=-20.5245 StartY=-0.740081 StartZ=0 EndX=-20.5245 EndY=4.25992 EndZ=0
  constraints (9):
    c: Coincident(g0,g1)
    c: Coincident(g1,g2)
    c: Coincident(g2,g3)
    c: Coincident(g3,g0)
    c: Horizontal(g0)
    c: Horizontal(g2)
    c: Vertical(g1)
    c: Vertical(g3)
    c: DistanceY(g3,g3) = 5
FEATURE [PartDesign::Pocket] Pocket023
  BaseFeature = -> Pocket022
  Direction = (0,-1,-2e-16)
  Length = 2
  Length2 = 5
  Placement = pos=(0,0,0) rot=(1,0,0;1.5708rad)
  Profile = -> Sketch036
  ReferenceAxis = -> Sketch036 [N_Axis]
  Refine = true
  Suppressed = false
  Type = 0
FEATURE [PartDesign::Body] Body004  label="Shim"
  AllowCompound = false
  Group = -> [Sketch034,Pad010,Sketch035,Pocket022,Sketch036,Pocket023]
  Origin = -> Origin006
  Placement = pos=(-2.5,-18,1.5) rot=(0,0,1;0rad)
  Tip = -> Pocket023
FEATURE [Sketcher::SketchObject] Sketch037
  ArcFitTolerance = 1e-06
  AttachmentSupport = -> [Pocket017]
  ExternalGeometry = -> [Pocket017]
  FullyConstrained = false
  MakeInternals = false
  MapMode = 5
  Placement = pos=(0,14.4346,-3.2e-15) rot=(-1,0,0;1.5708rad)
  sketch-geometry (8):
    g0: LineSegment StartX=-3.61502 StartY=32.1403 StartZ=0 EndX=-3.61502 EndY=28.4508 EndZ=0
    g1: LineSegment StartX=-3.61502 StartY=28.4508 StartZ=0 EndX=3.63498 EndY=28.4508 EndZ=0
    g2: LineSegment StartX=3.63498 StartY=28.4508 StartZ=0 EndX=3.63498 EndY=32.1403 EndZ=0
    g3: LineSegment StartX=3.63498 StartY=32.1403 StartZ=0 EndX=-3.61502 EndY=32.1403 EndZ=0
    g4: LineSegment StartX=3.63498 StartY=-26.6944 StartZ=0 EndX=-3.61502 EndY=-26.6944 EndZ=0
    g5: LineSegment StartX=-3.61502 StartY=-26.6944 StartZ=0 EndX=-3.61502 EndY=-29.7062 EndZ=0
    g6: LineSegment StartX=-3.61502 StartY=-29.7062 StartZ=0 EndX=3.63498 EndY=-29.7062 EndZ=0
    g7: LineSegment StartX=3.63498 StartY=-29.7062 StartZ=0 EndX=3.63498 EndY=-26.6944 EndZ=0
  constraints (20):
    c: Coincident(g0,g1)
    c: Coincident(g1,g2)
    c: Coincident(g2,g3)
    c: Coincident(g3,g0)
    c: Vertical(g0)
    c: Vertical(g2)
    c: Horizontal(g1)
    c: Horizontal(g3)
    c: PointOnObject(g0,g-4)
    c: PointOnObject(g1,g-3)
    c: Coincident(g4,g5)
    c: Coincident(g5,g6)
    c: Coincident(g6,g7)
    c: Coincident(g7,g4)
    c: Horizontal(g4)
    c: Horizontal(g6)
    c: Vertical(g5)
    c: Vertical(g7)
    c: PointOnObject(g4,g-3)
    c: PointOnObject(g5,g-4)
FEATURE [PartDesign::Pad] Pad011
  BaseFeature = -> Pocket017
  Direction = (0,1,2e-16)
  Length = 7
  Length2 = 10
  Placement = pos=(0,0,0) rot=(1,0,0;1.5708rad)
  Profile = -> Sketch037
  ReferenceAxis = -> Sketch037 [N_Axis]
  Refine = true
  Suppressed = false
  Type = 0
FEATURE [PartDesign::Body] Body001  label="PlotterHead"
  AllowCompound = false
  Group = -> [Sketch003,Pad001,Sketch004,Pocket002,Sketch005,Pad002,Sketch006,Pocket003,Sketch007,Pad003,Sketch008,Pocket004,Sketch009,Pocket005,Sketch010,Pocket006,LinearPattern,Sketch011,Pocket007,Sketch012,Pad004,Sketch013,Pocket008,LinearPattern001,Sketch014,Pocket009,LinearPattern002,Sketch015,Pocket010,LinearPattern003,Sketch016,Pocket011,LinearPattern004,Sketch017,Sketch018,Pocket012,Pocket013,Sketch020,+16 more]
  Origin = -> Origin003
  Placement = pos=(0,-14.5,0) rot=(0,0,1;0rad)
  Tip = -> Pad011
